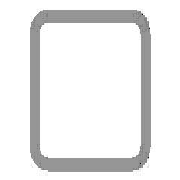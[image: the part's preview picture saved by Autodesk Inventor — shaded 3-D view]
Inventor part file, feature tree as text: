
AUTODESK INVENTOR PART (.ipt)
format: ipt  version: 2024 (Build 280153000, 153)  size: 164,352 bytes
history: native  units: mm (DEFAULTED — no unit token found)
features: plane x5, other x4, split x4, extrude x1, sketch x1
ambient origin geometry x8: Origin, YZ Plane, XZ Plane, XY Plane, X Axis, Y Axis, Z Axis, Center Point
bodies: Solid1 (feature_tree)
feature tree (15):
  parser-record x1  (decoder bookkeeping rows leaked as tree rows — omitted from the tree; the rows remain in map.json)
  other  "Driven Length"
  other  "Plano inicial"
  other  "Plano final"
  extrude  "Cuerpo"  TaperAngle=0.0deg  [1 undecoded]
  plane  "Plano de trabajo4"
  split  "Dividir1"
  plane  "Plano de trabajo5"
  split  "Dividir2"
  plane  "Plano de trabajo6"
  split  "Dividir3"
  plane  "Plano de trabajo7"
  split  "Dividir4"
  sketch  "Sketch3"  dims[d3=2237.080256mm d4=0.0mm d10=50.8mm d11=50.8mm d12=3.175mm d13=-23.540128mm d14=2213.540128mm d15=25.4mm d16=25.4mm d17=6.35mm d18=90.0deg d19=2237.080256mm]
  plane  "Work Plane3"
note: 1 required parameter value undecoded (feature->parameter linkage not recoverable at this tier; creation-order binding heuristic only, values carry confidence <= 0.55)
